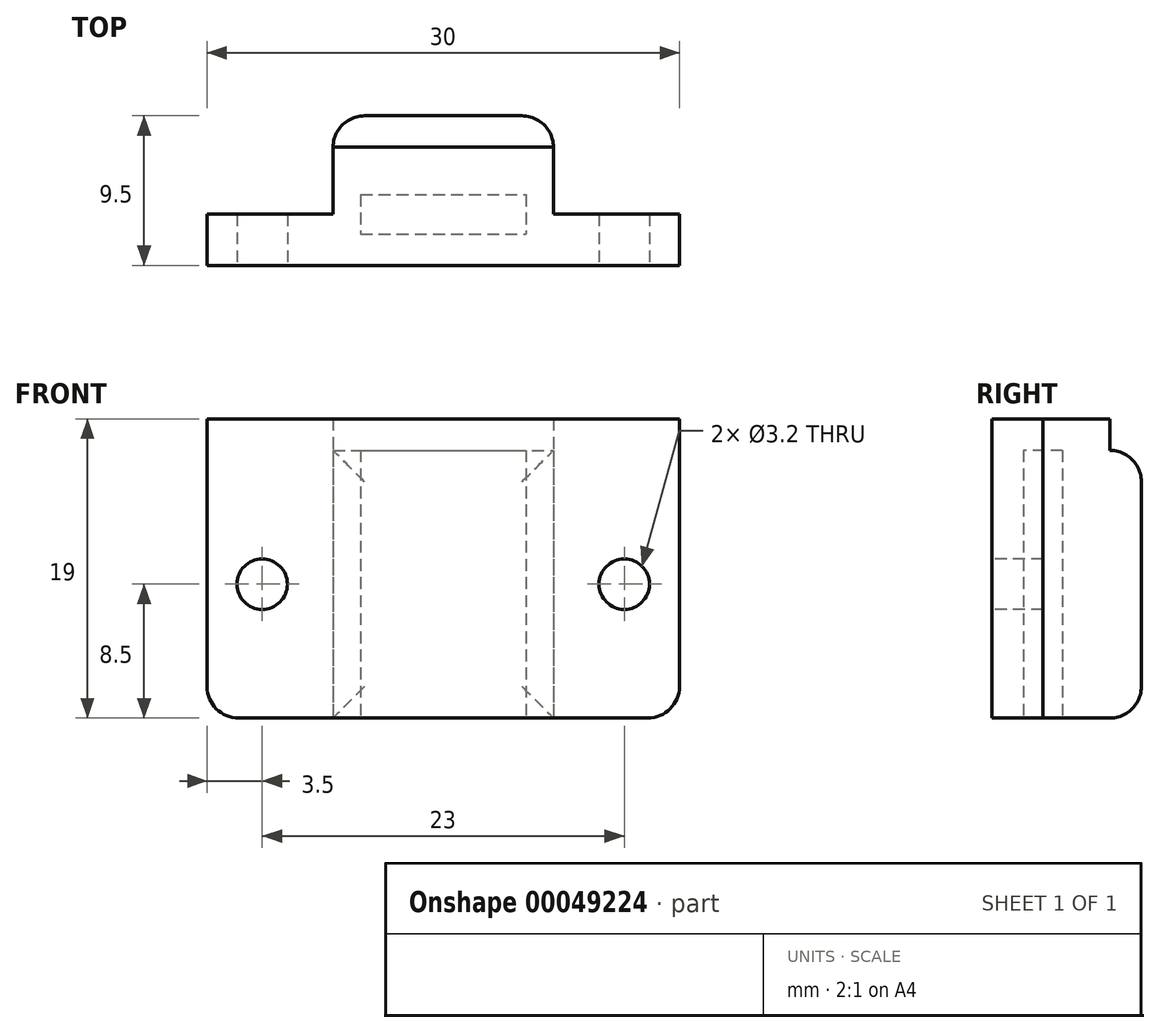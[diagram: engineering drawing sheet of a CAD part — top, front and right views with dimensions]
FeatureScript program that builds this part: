
annotation { "Feature Type Name" : "Feature", "Feature Type Description" : "" }
export const myFeature = defineFeature(function(context is Context, id is Id, definition is map)
    precondition{}
    {
        {
            var Q0;
            Q0=qCreatedBy(makeId("Top.planeOp"),FACE);
            var sketch = newSketch(context, id + "F0", { "sketchPlane" : qUnion([Q0])});
            skLineSegment(sketch, "E0.bottom", {"start": v(-7, 5) * mm, "end": v(7, 5) * mm});
            skLineSegment(sketch, "E0.top", {"start": v(-7, -4.5) * mm, "end": v(7, -4.5) * mm});
            skLineSegment(sketch, "E0.left", {"start": v(-7, 5) * mm, "end": v(-7, -4.5) * mm});
            skLineSegment(sketch, "E0.right", {"start": v(7, 5) * mm, "end": v(7, -4.5) * mm});
            skLineSegment(sketch, "E1.bottom", {"start": v(-5.25, 0) * mm, "end": v(5.25, 0) * mm});
            skLineSegment(sketch, "E1.top", {"start": v(-5.25, -2.5) * mm, "end": v(5.25, -2.5) * mm});
            skLineSegment(sketch, "E1.left", {"start": v(-5.25, 0) * mm, "end": v(-5.25, -2.5) * mm});
            skLineSegment(sketch, "E1.right", {"start": v(5.25, 0) * mm, "end": v(5.25, -2.5) * mm});
            skLineSegment(sketch, "E2", {"start": v(5.25, -1.25) * mm, "end": v(7, -1.25) * mm, "construction": true});
            skLineSegment(sketch, "E3", {"start": v(-5.25, -1.25) * mm, "end": v(-7, -1.25) * mm, "construction": true});
            skLineSegment(sketch, "E4", {"start": v(0, 0) * mm, "end": v(0, 5) * mm, "construction": true});
            skLineSegment(sketch, "E5.bottom", {"start": v(-7, -1.25) * mm, "end": v(-15, -1.25) * mm});
            skLineSegment(sketch, "E5.top", {"start": v(-7, -4.5) * mm, "end": v(-15, -4.5) * mm});
            skLineSegment(sketch, "E5.left", {"start": v(-7, -1.25) * mm, "end": v(-7, -4.5) * mm});
            skLineSegment(sketch, "E5.right", {"start": v(-15, -1.25) * mm, "end": v(-15, -4.5) * mm});
            skLineSegment(sketch, "E6.bottom", {"start": v(7, -1.25) * mm, "end": v(15, -1.25) * mm});
            skLineSegment(sketch, "E6.top", {"start": v(7, -4.5) * mm, "end": v(15, -4.5) * mm});
            skLineSegment(sketch, "E6.left", {"start": v(7, -1.25) * mm, "end": v(7, -4.5) * mm});
            skLineSegment(sketch, "E6.right", {"start": v(15, -1.25) * mm, "end": v(15, -4.5) * mm});
            skSolve(sketch);
        }
        {
            var Q0;
            Q0=makeQuery(id+"F0.imprint","IMPRINT",FACE,{"disambiguationData":[TD([[makeQuery(id+"F0.imprint","IMPRINT",EDGE,{"derivedFrom":sQuery(id+"F0.wireOp",EDGE,"E0.bottom")}),-1.0]])]});
            var Q1;
            Q1=makeQuery(id+"F0.imprint","IMPRINT",FACE,{"disambiguationData":[TD([[makeQuery(id+"F0.imprint","IMPRINT",EDGE,{"derivedFrom":sQuery(id+"F0.wireOp",EDGE,"E6.bottom")}),-1.0]])]});
            var Q2;
            Q2=makeQuery(id+"F0.imprint","IMPRINT",FACE,{"disambiguationData":[TD([[makeQuery(id+"F0.imprint","IMPRINT",EDGE,{"derivedFrom":sQuery(id+"F0.wireOp",EDGE,"E5.bottom")}),1.0]])]});
            extrude(context, id + "F1", {"entities" : qUnion([Q0, Q1, Q2]), "depth" : 17 * mm, "offsetDistance" : 25 * mm});
        }
        {
            var Q0;
            Q0=makeQuery(id+"F1.opExtrude","SWEPT_FACE",FACE,{"disambiguationData":[OSD([sQuery(id+"F0.wireOp",EDGE,"E0.top"),sQuery(id+"F0.wireOp",EDGE,"E5.top"),sQuery(id+"F0.wireOp",EDGE,"E6.top")])]});
            var sketch = newSketch(context, id + "F2", { "sketchPlane" : qUnion([Q0])});
            skCircle(sketch, "E7", {"center": v(11.5, 8.5) * mm, "radius": 1.6 * mm});
            skCircle(sketch, "E8", {"center": v(-11.5, 8.5) * mm, "radius": 1.6 * mm});
            skLineSegment(sketch, "E9", {"start": v(-11.5, 8.5) * mm, "end": v(-11.5, 17) * mm, "construction": true});
            skLineSegment(sketch, "E10", {"start": v(-11.5, 8.5) * mm, "end": v(-11.5, 0) * mm, "construction": true});
            skLineSegment(sketch, "E11", {"start": v(-11.5, 8.5) * mm, "end": v(-15, 8.5) * mm, "construction": true});
            skLineSegment(sketch, "E12", {"start": v(11.5, 8.5) * mm, "end": v(15, 8.5) * mm, "construction": true});
            skSolve(sketch);
        }
        {
            var Q0;
            Q0 = qSketchRegion(id + "F2", true);
            extrude(context, id + "F3", {"entities" : qUnion([Q0]), "operationType" : NewBodyOperationType.REMOVE, "oppositeDirection" : true, "depth" : 25 * mm, "offsetDistance" : 25 * mm});
        }
        {
            var Q0;
            Q0=makeQuery(id+"F1.opExtrude","CAP_EDGE",EDGE,{"disambiguationData":[OSD([sQuery(id+"F0.wireOp",EDGE,"E0.bottom")])],"isStart":true});
            var Q1;
            Q1=makeQuery(id+"F1.opExtrude","SWEPT_EDGE",EDGE,{"disambiguationData":[OSD([sQuery(id+"F0.wireOp",EDGE,"E0.bottom"),sQuery(id+"F0.wireOp",EDGE,"E0.left")])]});
            var Q2;
            Q2=makeQuery(id+"F1.opExtrude","CAP_EDGE",EDGE,{"disambiguationData":[OSD([sQuery(id+"F0.wireOp",EDGE,"E0.bottom")])],"isStart":false});
            var Q3;
            Q3=makeQuery(id+"F1.opExtrude","SWEPT_EDGE",EDGE,{"disambiguationData":[OSD([sQuery(id+"F0.wireOp",EDGE,"E0.bottom"),sQuery(id+"F0.wireOp",EDGE,"E0.right")])]});
            var Q4;
            Q4=makeQuery(id+"F1.opExtrude","CAP_EDGE",EDGE,{"disambiguationData":[OSD([sQuery(id+"F0.wireOp",EDGE,"E5.right")])],"isStart":true});
            var Q5;
            Q5=makeQuery(id+"F1.opExtrude","CAP_EDGE",EDGE,{"disambiguationData":[OSD([sQuery(id+"F0.wireOp",EDGE,"E6.right")])],"isStart":true});
            fillet(context, id + "F4", {"entities" : qUnion([Q0, Q1, Q2, Q3, Q4, Q5]), "radius" : 2 * mm, "tangentPropagation" : true, "allowEdgeOverflow" : false});
        }
        {
            var Q0;
            Q0=makeQuery(id+"F1.opExtrude","CAP_FACE",FACE,{"disambiguationData":[OSD([sQuery(id+"F0.wireOp",EDGE,"E0.bottom"),sQuery(id+"F0.wireOp",EDGE,"E0.top"),sQuery(id+"F0.wireOp",EDGE,"E0.left"),sQuery(id+"F0.wireOp",EDGE,"E0.right"),sQuery(id+"F0.wireOp",EDGE,"E1.bottom"),sQuery(id+"F0.wireOp",EDGE,"E1.top"),sQuery(id+"F0.wireOp",EDGE,"E1.left"),sQuery(id+"F0.wireOp",EDGE,"E1.right"),sQuery(id+"F0.wireOp",EDGE,"E5.bottom"),sQuery(id+"F0.wireOp",EDGE,"E5.top"),sQuery(id+"F0.wireOp",EDGE,"E5.right"),sQuery(id+"F0.wireOp",EDGE,"E6.bottom"),sQuery(id+"F0.wireOp",EDGE,"E6.top"),sQuery(id+"F0.wireOp",EDGE,"E6.right")])],"isStart":false});
            var sketch = newSketch(context, id + "F5", { "sketchPlane" : qUnion([Q0])});
            skLineSegment(sketch, "E13", {"start": v(-15, -1.25) * mm, "end": v(-7, -1.25) * mm});
            skLineSegment(sketch, "E14", {"start": v(-7, -1.25) * mm, "end": v(-7, 3) * mm});
            skLineSegment(sketch, "E15", {"start": v(-7, 3) * mm, "end": v(7, 3) * mm});
            skLineSegment(sketch, "E16", {"start": v(7, 3) * mm, "end": v(7, -1.25) * mm});
            skLineSegment(sketch, "E17", {"start": v(7, -1.25) * mm, "end": v(15, -1.25) * mm});
            skLineSegment(sketch, "E18", {"start": v(15, -1.25) * mm, "end": v(15, -4.5) * mm});
            skLineSegment(sketch, "E19", {"start": v(15, -4.5) * mm, "end": v(-15, -4.5) * mm});
            skLineSegment(sketch, "E20", {"start": v(-15, -4.5) * mm, "end": v(-15, -1.25) * mm});
            skSolve(sketch);
        }
        {
            var Q0;
            Q0=makeQuery(id+"F5.imprint","IMPRINT",FACE,{"disambiguationData":[TD([[makeQuery(id+"F5.imprint","IMPRINT",EDGE,{"derivedFrom":makeQuery(id+"F1.opExtrude","CAP_EDGE",EDGE,{"disambiguationData":[OSD([sQuery(id+"F0.wireOp",EDGE,"E1.bottom")])],"isStart":false})}),-1.0]])]});
            var Q1;
            Q1=makeQuery(id+"F5.imprint","IMPRINT",FACE,{"disambiguationData":[TD([[makeQuery(id+"F5.imprint","IMPRINT",EDGE,{"derivedFrom":sQuery(id+"F5.wireOp",EDGE,"E13")}),1.0]])]});
            extrude(context, id + "F6", {"entities" : qUnion([Q0, Q1]), "operationType" : NewBodyOperationType.ADD, "depth" : 2 * mm, "offsetDistance" : 25 * mm});
        }
    });
